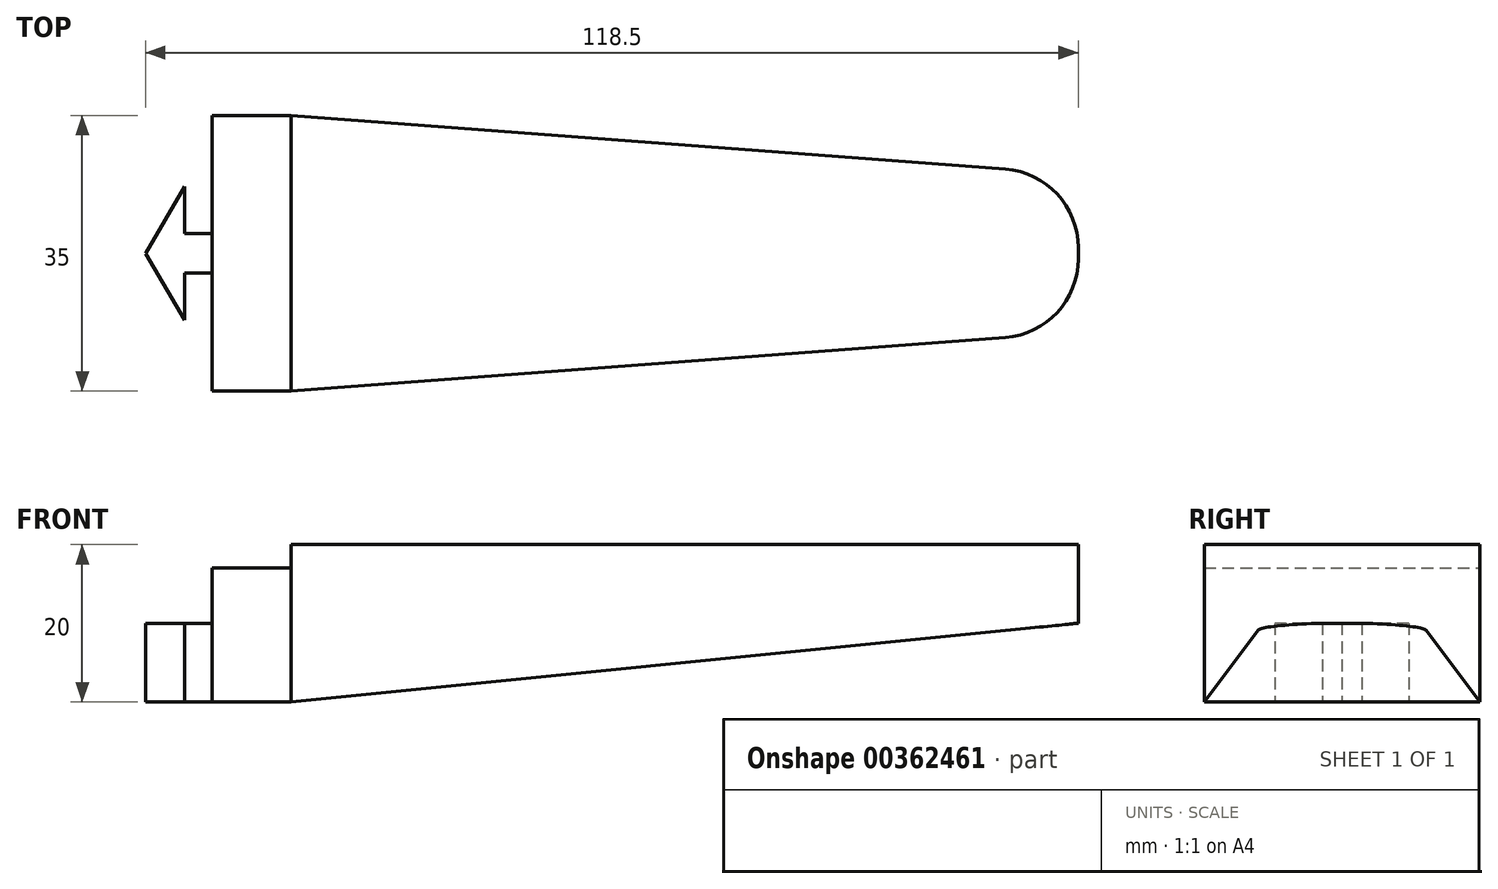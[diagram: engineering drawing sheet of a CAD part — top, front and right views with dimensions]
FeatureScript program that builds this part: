
annotation { "Feature Type Name" : "Feature", "Feature Type Description" : "" }
export const myFeature = defineFeature(function(context is Context, id is Id, definition is map)
    precondition{}
    {
        {
            var Q0;
            Q0=qCreatedBy(makeId("Top.planeOp"),FACE);
            var sketch = newSketch(context, id + "F0", { "sketchPlane" : qUnion([Q0])});
            skLineSegment(sketch, "E0.bottom", {"start": v(55, -17.5) * mm, "end": v(-55, -17.5) * mm});
            skLineSegment(sketch, "E0.top", {"start": v(55, 17.5) * mm, "end": v(-55, 17.5) * mm});
            skLineSegment(sketch, "E0.left", {"start": v(55, -17.5) * mm, "end": v(55, 17.5) * mm});
            skLineSegment(sketch, "E0.right", {"start": v(-55, -17.5) * mm, "end": v(-55, 17.5) * mm});
            skPoint(sketch, "E0.middle", {"position": v(0, 0) * mm});
            skLineSegment(sketch, "E1.bottom", {"start": v(-55, -2.5) * mm, "end": v(-58.5, -2.5) * mm});
            skLineSegment(sketch, "E1.top", {"start": v(-55, 2.5) * mm, "end": v(-58.5, 2.5) * mm});
            skLineSegment(sketch, "E1.left", {"start": v(-55, -2.5) * mm, "end": v(-55, 2.5) * mm});
            skLineSegment(sketch, "E1.right", {"start": v(-58.5, -2.5) * mm, "end": v(-58.5, 2.5) * mm});
            skPoint(sketch, "E1.middle", {"position": v(-56.75, 0) * mm});
            skPoint(sketch, "E2", {"position": v(-58.5, 8.5) * mm});
            skPoint(sketch, "E3", {"position": v(-58.5, -8.5) * mm});
            skPoint(sketch, "E4", {"position": v(-58.5, 0) * mm});
            skLineSegment(sketch, "E5", {"start": v(-58.5, 0) * mm, "end": v(-58.5, 8.5) * mm});
            skLineSegment(sketch, "E6", {"start": v(-58.5, 0) * mm, "end": v(-58.5, -8.5) * mm});
            skPoint(sketch, "E7", {"position": v(-63.5, 0) * mm});
            skLineSegment(sketch, "E8", {"start": v(-58.5, 8.5) * mm, "end": v(-63.5, 0) * mm});
            skLineSegment(sketch, "E9", {"start": v(-58.5, -8.5) * mm, "end": v(-63.5, 0) * mm});
            skSolve(sketch);
        }
        {
            var Q0;
            {var subQ6=sQuery(id+"F0.wireOp",EDGE,"E8");Q0=makeQuery(id+"F0.imprint","IMPRINT",FACE,{"disambiguationData":[TD([[makeQuery(id+"F0.imprint","IMPRINT",EDGE,{"derivedFrom":subQ6}),1.0]])]});}
            var Q1;
            {var subQ4=sQuery(id+"F0.wireOp",EDGE,"E1.bottom");Q1=makeQuery(id+"F0.imprint","IMPRINT",FACE,{"disambiguationData":[TD([[makeQuery(id+"F0.imprint","IMPRINT",EDGE,{"derivedFrom":subQ4}),-1.0]])]});}
            extrude(context, id + "F1", {"entities" : qUnion([Q0, Q1]), "depth" : 10 * mm});
        }
        {
            var Q0;
            {var subQ1=sQuery(id+"F0.wireOp",EDGE,"E0.bottom");Q0=makeQuery(id+"F0.imprint","IMPRINT",FACE,{"disambiguationData":[TD([[makeQuery(id+"F0.imprint","IMPRINT",EDGE,{"derivedFrom":subQ1}),-1.0]])]});}
            extrude(context, id + "F2", {"entities" : qUnion([Q0]), "operationType" : NewBodyOperationType.ADD, "depth" : 17 * mm});
        }
        {
            var Q0;
            Q0=makeQuery(id+"F2.opExtrude","CAP_FACE",FACE,{"disambiguationData":[OSD([sQuery(id+"F0.wireOp",EDGE,"E0.bottom"),sQuery(id+"F0.wireOp",EDGE,"E0.top"),sQuery(id+"F0.wireOp",EDGE,"E0.left"),sQuery(id+"F0.wireOp",EDGE,"E0.right"),sQuery(id+"F0.wireOp",EDGE,"E1.left")])],"isStart":false});
            var sketch = newSketch(context, id + "F3", { "sketchPlane" : qUnion([Q0])});
            skLineSegment(sketch, "E10.bottom", {"start": v(55, 17.5) * mm, "end": v(-45, 17.5) * mm});
            skLineSegment(sketch, "E10.top", {"start": v(55, -17.5) * mm, "end": v(-45, -17.5) * mm});
            skLineSegment(sketch, "E10.left", {"start": v(55, 17.5) * mm, "end": v(55, -17.5) * mm});
            skLineSegment(sketch, "E10.right", {"start": v(-45, 17.5) * mm, "end": v(-45, -17.5) * mm});
            skSolve(sketch);
        }
        {
            var Q0;
            Q0=makeQuery(id+"F3.imprint","IMPRINT",FACE,{"disambiguationData":[TD([[makeQuery(id+"F3.imprint","IMPRINT",EDGE,{"derivedFrom":sQuery(id+"F3.wireOp",EDGE,"E10.bottom")}),1.0]])]});
            extrude(context, id + "F4", {"entities" : qUnion([Q0]), "operationType" : NewBodyOperationType.ADD, "depth" : 3 * mm});
        }
        {
            var Q0;
            Q0=makeQuery(id+"F2.opExtrude","CAP_EDGE",EDGE,{"disambiguationData":[OSD([sQuery(id+"F0.wireOp",EDGE,"E0.left")])],"isStart":true});
            chamfer(context, id + "F5", {"entities" : qUnion([Q0]), "chamferType" : ChamferType.TWO_OFFSETS, "width1" : 100 * mm, "oppositeDirection" : true, "width2" : 10 * mm, "tangentPropagation" : true});
        }
        {
            var Q0;
            Q0=makeQuery(id+"F4.boolean.opBoolean","MERGE",EDGE,{"derivedFrom":[makeQuery(id+"F2.opExtrude","SWEPT_EDGE",EDGE,{"disambiguationData":[OSD([sQuery(id+"F0.wireOp",EDGE,"E0.bottom"),sQuery(id+"F0.wireOp",EDGE,"E0.left")])]}),makeQuery(id+"F4.opExtrude","SWEPT_EDGE",EDGE,{"disambiguationData":[OSD([sQuery(id+"F3.wireOp",EDGE,"E10.top"),sQuery(id+"F3.wireOp",EDGE,"E10.left")])]})]});
            var Q1;
            Q1=makeQuery(id+"F4.boolean.opBoolean","MERGE",EDGE,{"derivedFrom":[makeQuery(id+"F2.opExtrude","SWEPT_EDGE",EDGE,{"disambiguationData":[OSD([sQuery(id+"F0.wireOp",EDGE,"E0.top"),sQuery(id+"F0.wireOp",EDGE,"E0.left")])]}),makeQuery(id+"F4.opExtrude","SWEPT_EDGE",EDGE,{"disambiguationData":[OSD([sQuery(id+"F3.wireOp",EDGE,"E10.bottom"),sQuery(id+"F3.wireOp",EDGE,"E10.left")])]})]});
            chamfer(context, id + "F6", {"entities" : qUnion([Q0, Q1]), "chamferType" : ChamferType.TWO_OFFSETS, "width1" : 7.5 * mm, "oppositeDirection" : false, "width2" : 100 * mm, "tangentPropagation" : true});
        }
        {
            var Q0;
            {var subQ0=sQuery(id+"F3.wireOp",EDGE,"E10.left");var subQ1=sQuery(id+"F0.wireOp",EDGE,"E0.left");Q0=makeQuery(id+"F6.opChamfer","BLEND_EDGE",EDGE,{"blendedFrom":[makeQuery(id+"F4.boolean.opBoolean","MERGE",EDGE,{"derivedFrom":[makeQuery(id+"F2.opExtrude","SWEPT_EDGE",EDGE,{"disambiguationData":[OSD([sQuery(id+"F0.wireOp",EDGE,"E0.bottom"),subQ1])]}),makeQuery(id+"F4.opExtrude","SWEPT_EDGE",EDGE,{"disambiguationData":[OSD([sQuery(id+"F3.wireOp",EDGE,"E10.top"),subQ0])]})]}),makeQuery(id+"F4.boolean.opBoolean","MERGE",FACE,{"derivedFrom":[makeQuery(id+"F2.opExtrude","SWEPT_FACE",FACE,{"disambiguationData":[OSD([subQ1])]}),makeQuery(id+"F4.opExtrude","SWEPT_FACE",FACE,{"disambiguationData":[OSD([subQ0])]})]})],"blendedInto":[makeQuery(id+"F4.boolean.opBoolean","MERGE",FACE,{"derivedFrom":[makeQuery(id+"F2.opExtrude","SWEPT_FACE",FACE,{"disambiguationData":[OSD([subQ1])]}),makeQuery(id+"F4.opExtrude","SWEPT_FACE",FACE,{"disambiguationData":[OSD([subQ0])]})]})]});}
            var Q1;
            {var subQ0=sQuery(id+"F3.wireOp",EDGE,"E10.left");var subQ1=sQuery(id+"F0.wireOp",EDGE,"E0.left");Q1=makeQuery(id+"F6.opChamfer","BLEND_EDGE",EDGE,{"blendedFrom":[makeQuery(id+"F4.boolean.opBoolean","MERGE",EDGE,{"derivedFrom":[makeQuery(id+"F2.opExtrude","SWEPT_EDGE",EDGE,{"disambiguationData":[OSD([sQuery(id+"F0.wireOp",EDGE,"E0.top"),subQ1])]}),makeQuery(id+"F4.opExtrude","SWEPT_EDGE",EDGE,{"disambiguationData":[OSD([sQuery(id+"F3.wireOp",EDGE,"E10.bottom"),subQ0])]})]}),makeQuery(id+"F4.boolean.opBoolean","MERGE",FACE,{"derivedFrom":[makeQuery(id+"F2.opExtrude","SWEPT_FACE",FACE,{"disambiguationData":[OSD([subQ1])]}),makeQuery(id+"F4.opExtrude","SWEPT_FACE",FACE,{"disambiguationData":[OSD([subQ0])]})]})],"blendedInto":[makeQuery(id+"F4.boolean.opBoolean","MERGE",FACE,{"derivedFrom":[makeQuery(id+"F2.opExtrude","SWEPT_FACE",FACE,{"disambiguationData":[OSD([subQ1])]}),makeQuery(id+"F4.opExtrude","SWEPT_FACE",FACE,{"disambiguationData":[OSD([subQ0])]})]})]});}
            fillet(context, id + "F7", {"entities" : qUnion([Q0, Q1]), "radius" : 10 * mm, "tangentPropagation" : true, "allowEdgeOverflow" : false});
        }
    });
